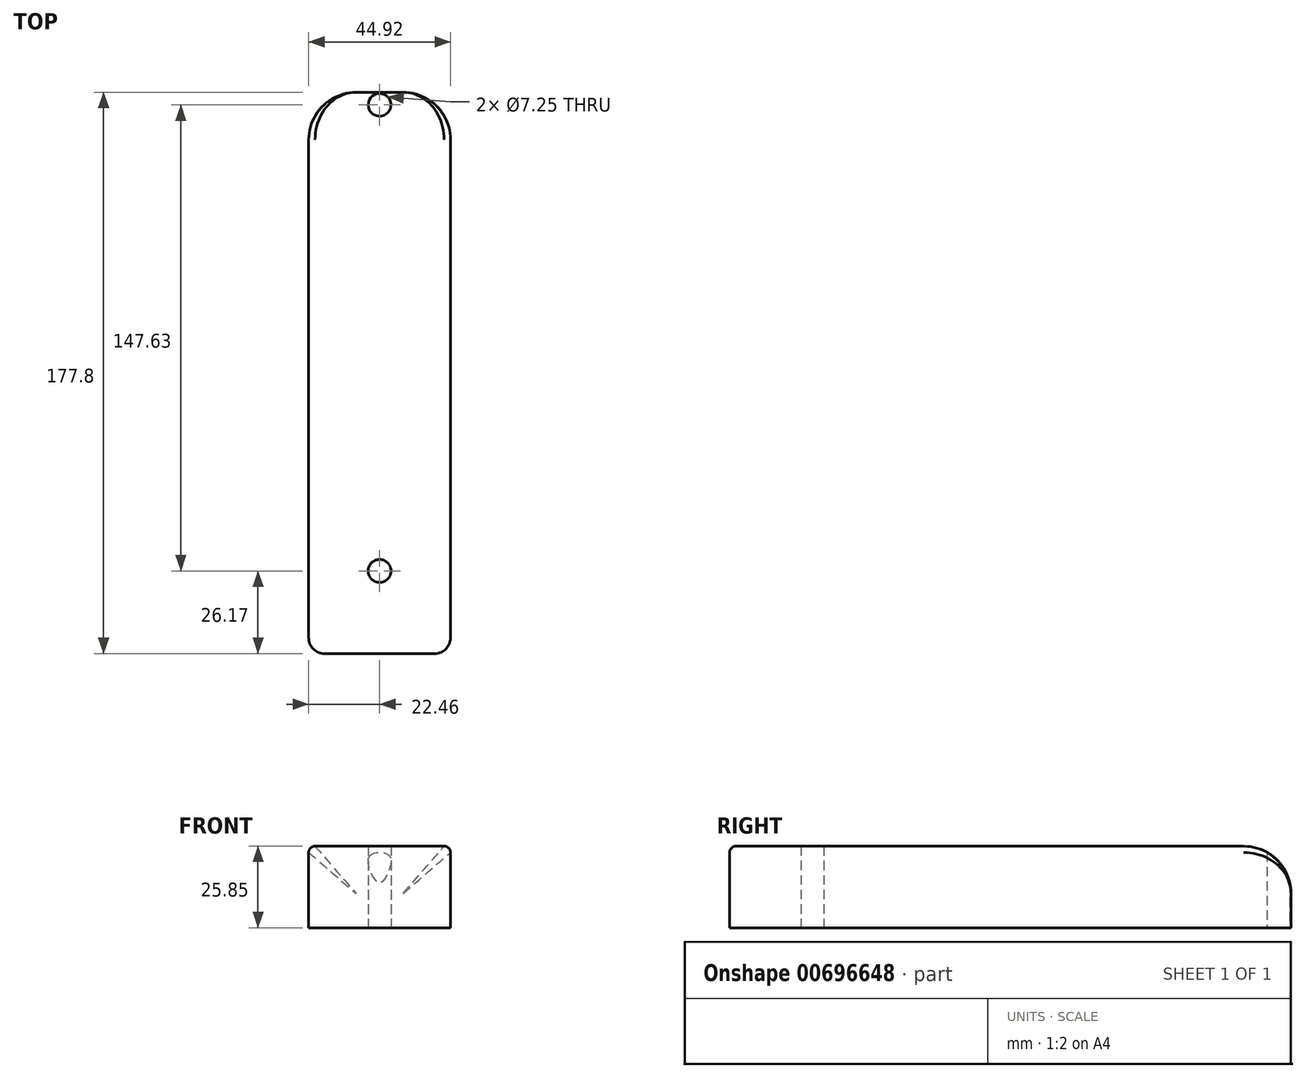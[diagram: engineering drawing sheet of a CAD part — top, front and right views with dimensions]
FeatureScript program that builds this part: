
annotation { "Feature Type Name" : "Feature", "Feature Type Description" : "" }
export const myFeature = defineFeature(function(context is Context, id is Id, definition is map)
    precondition{}
    {
        {
            var Q0;
            Q0=qCreatedBy(makeId("Top.planeOp"),FACE);
            var sketch = newSketch(context, id + "F0", { "sketchPlane" : qUnion([Q0])});
            skLineSegment(sketch, "E0.bottom", {"start": v(22.46, 88.9) * mm, "end": v(-22.46, 88.9) * mm});
            skLineSegment(sketch, "E0.top", {"start": v(22.47, -88.9) * mm, "end": v(-22.46, -88.9) * mm});
            skLineSegment(sketch, "E0.left", {"start": v(22.46, 88.9) * mm, "end": v(22.46, -88.9) * mm});
            skLineSegment(sketch, "E0.right", {"start": v(-22.46, 88.9) * mm, "end": v(-22.47, -88.9) * mm});
            skPoint(sketch, "E0.middle", {"position": v(0, 0) * mm});
            skLineSegment(sketch, "E1", {"start": v(0, -88.9) * mm, "end": v(0, -62.73) * mm, "construction": true});
            skCircle(sketch, "E2", {"center": v(0, -62.73) * mm, "radius": 3.62 * mm});
            skLineSegment(sketch, "E3", {"start": v(0, 88.9) * mm, "end": v(0, 84.9) * mm, "construction": true});
            skCircle(sketch, "E4", {"center": v(0, 84.9) * mm, "radius": 3.62 * mm});
            skSolve(sketch);
        }
        {
            var Q0;
            Q0 = qSketchRegion(id + "F0", true);
            extrude(context, id + "F1", {"entities" : qUnion([Q0]), "depth" : 25.85 * mm, "offsetDistance" : 25 * mm});
        }
        {
            var Q0;
            Q0=makeQuery(id+"F1.opExtrude","CAP_EDGE",EDGE,{"disambiguationData":[OSD([sQuery(id+"F0.wireOp",EDGE,"E0.right")])],"isStart":false});
            var Q1;
            Q1=makeQuery(id+"F1.opExtrude","CAP_EDGE",EDGE,{"disambiguationData":[OSD([sQuery(id+"F0.wireOp",EDGE,"E0.left")])],"isStart":false});
            var Q2;
            Q2=makeQuery(id+"F1.opExtrude","CAP_EDGE",EDGE,{"disambiguationData":[OSD([sQuery(id+"F0.wireOp",EDGE,"E0.top")])],"isStart":false});
            fillet(context, id + "F2", {"entities" : qUnion([Q0, Q1, Q2]), "radius" : 2 * mm, "tangentPropagation" : true, "allowEdgeOverflow" : false});
        }
        {
            var Q0;
            Q0=makeQuery(id+"F1.opExtrude","SWEPT_EDGE",EDGE,{"disambiguationData":[OSD([sQuery(id+"F0.wireOp",EDGE,"E0.top"),sQuery(id+"F0.wireOp",EDGE,"E0.right")])]});
            var Q1;
            Q1=makeQuery(id+"F1.opExtrude","SWEPT_EDGE",EDGE,{"disambiguationData":[OSD([sQuery(id+"F0.wireOp",EDGE,"E0.top"),sQuery(id+"F0.wireOp",EDGE,"E0.left")])]});
            fillet(context, id + "F3", {"entities" : qUnion([Q0, Q1]), "radius" : 5 * mm, "tangentPropagation" : true, "allowEdgeOverflow" : false});
        }
        {
            var Q0;
            Q0=makeQuery(id+"F1.opExtrude","CAP_EDGE",EDGE,{"disambiguationData":[OSD([sQuery(id+"F0.wireOp",EDGE,"E0.bottom")])],"isStart":false});
            fillet(context, id + "F4", {"entities" : qUnion([Q0]), "radius" : 15 * mm, "tangentPropagation" : true, "allowEdgeOverflow" : false});
        }
    });
